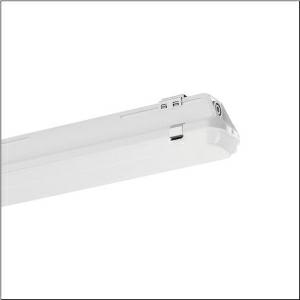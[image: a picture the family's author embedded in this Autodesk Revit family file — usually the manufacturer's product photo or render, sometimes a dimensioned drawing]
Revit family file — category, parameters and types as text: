
# Revit family: monsun_r__21_51fb10dp460b_c90e
name_source: partatom
category: Lighting Fixtures
units: mm (PartAtom-declared; Revit-internal decimal feet)

## family parameters
Cut with Voids When Loaded = No
Host = Face
Light Source = No
Part Type = Normal
Room Calculation Point = No
Round Connector Dimension = Use Diameter
Shared = No

## types (1)
- --- (1 x LED, 6060 lm, 39.4 W, 4000K)
    Apparent Load = 39 VA
    CIE Flux Codes = 47 77 93 94 100
    Color Rendering = 80
    Color Temperature = 4000K
    Default Elevation = 1800 mm
    Description = Monsun® 21, damp-proof luminaire, chain hanger, primary optical cover: enclosure, of PMMA, light emission: direct distribution, primary light characteristic: symmetric, installation type: suspended mounting, surface-mounted, horizontal mounting, vertical mounting, LED, rated luminous flux: 6.060lm, luminous efficacy: 154lm/W, light colour: 840, colour temperature: 4000K, control gear: ECG DALI, with terminal, 5-pole, max. 2.5mm², mains connection: 220..240V, AC, 50/60Hz, rated input power: 39W, housing, of glass-fibre reinforced polyester, uncoated, bright grey, length: 1.590mm, width: 90mm, height: 88mm, clip for enclosure, of stainless steel (V2A), ceiling mounting element, of stainless steel (V2A), chain hanger, of stainless steel (V2A), protection rating (complete): IP66, insulation class (complete): insulation class I (protective earthing), certification: CE, ENEC, VDE, UKCA, protection symbol: D, impact resistance: IK04, permissible operating ambient temperature: -25..+35°C, standard: EN 50419, EN 60598-2-1, corresponds to IFS (International Featured Standards) requirements for safety and quality in the food industry, for indoor or canopied outdoor use, no direct snow, no direct sun, no direct rain, packaging unit: 1 piece
    Height = 89 mm
    Lamp = 1 x LED
    Lamp Light Flux = 6060 lm
    Lamp Power = 39.4 W
    Lamp count = 1
    Length = 1590 mm
    Luminous efficacy = 154 lm/W
    Manufacturer = Siteco
    ModVariant = No
    Model = 51FB10DP460B
    Mounting Place = Ceiling
    Mounting Type = Pendant
    Number of Poles = 1
    OnlyDefault = Yes
    Power Factor = 1
    Product Name = Monsun® 21
    Product group = damp-proof luminaire | ceiling pendant
    ProductGroupID = 908
    Protection Class = Protection class I
    Protection Degree = IP 66
    RLX_Detail_Level = 1
    RlxData = <blob elided: 92077 chars, md5=469c0cb2>
    Socket = socket
    Standby Power = 0 W
    System Light Flux = 6060 lm
    System Power = 39 W
    Type Comments = factory setting: luminous flux: 100 % | dim-lin: 254 | 261 mA
    Type Image = l_1006717.jpg
    URL = http://relux.com
    VarID = @adj_125249
    Voltage = 0 V
    Weight = 0.00 kg
    Width = 90 mm

## geometry (parser evidence)
native form markers: Blend x4, Sweep x13
no freeform markers — native parametric forms only
